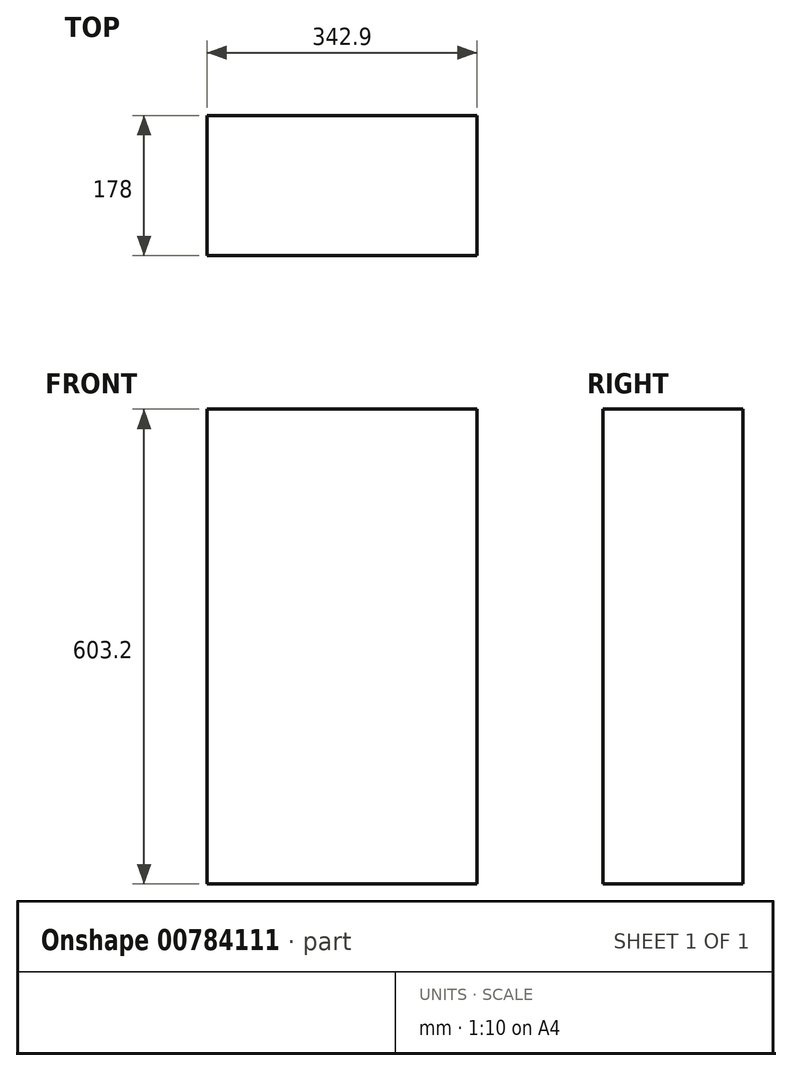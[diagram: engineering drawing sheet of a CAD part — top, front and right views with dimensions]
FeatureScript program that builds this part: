
annotation { "Feature Type Name" : "Feature", "Feature Type Description" : "" }
export const myFeature = defineFeature(function(context is Context, id is Id, definition is map)
    precondition{}
    {
        {
            var Q0;
            Q0=qCreatedBy(makeId("Front.planeOp"),FACE);
            var sketch = newSketch(context, id + "F0", { "sketchPlane" : qUnion([Q0])});
            skLineSegment(sketch, "E0.bottom", {"start": v(0, 0) * mm, "end": v(342.9, 0) * mm});
            skLineSegment(sketch, "E0.top", {"start": v(0, 603.2) * mm, "end": v(342.9, 603.2) * mm});
            skLineSegment(sketch, "E0.left", {"start": v(0, 0) * mm, "end": v(0, 603.2) * mm});
            skLineSegment(sketch, "E0.right", {"start": v(342.9, 0) * mm, "end": v(342.9, 603.2) * mm});
            skSolve(sketch);
        }
        {
            var Q0;
            Q0=makeQuery(id+"F0.imprint","IMPRINT",FACE,{"disambiguationData":[TD([[makeQuery(id+"F0.imprint","IMPRINT",EDGE,{"derivedFrom":sQuery(id+"F0.wireOp",EDGE,"E0.bottom")}),1.0]])]});
            extrude(context, id + "F1", {"entities" : qUnion([Q0]), "depth" : 178 * mm, "offsetDistance" : 25 * mm});
        }
    });
